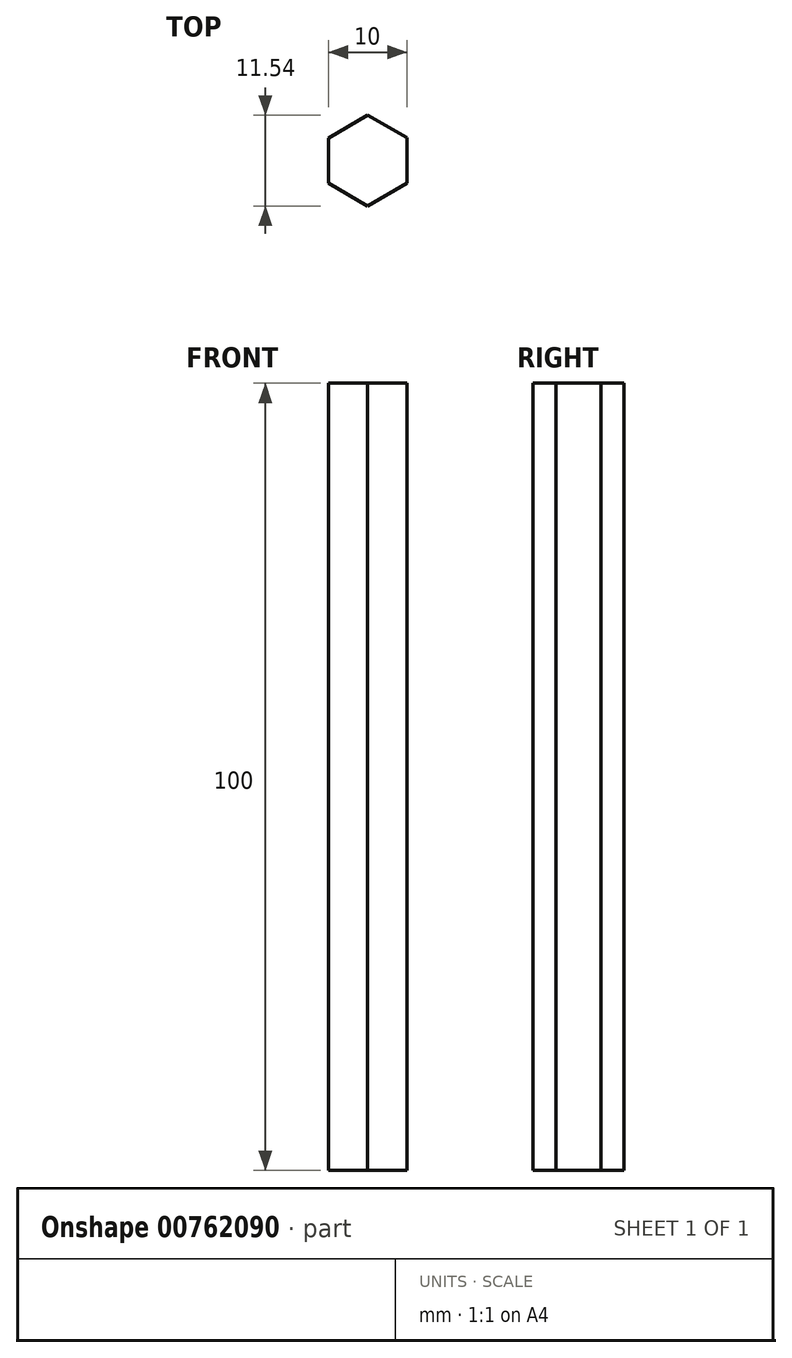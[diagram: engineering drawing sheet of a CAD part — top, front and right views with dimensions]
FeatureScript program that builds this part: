
annotation { "Feature Type Name" : "Feature", "Feature Type Description" : "" }
export const myFeature = defineFeature(function(context is Context, id is Id, definition is map)
    precondition{}
    {
        {
            var Q0;
            Q0=qCreatedBy(makeId("Top.planeOp"),FACE);
            var sketch = newSketch(context, id + "F0", { "sketchPlane" : qUnion([Q0])});
            skCircle(sketch, "E0.cCircle", {"center": v(0, 0) * mm, "radius": 5 * mm, "construction": true});
            skLineSegment(sketch, "E0.0", {"start": v(5, -2.88) * mm, "end": v(0, -5.77) * mm});
            skLineSegment(sketch, "E0.1", {"start": v(0, -5.77) * mm, "end": v(-5, -2.9) * mm});
            skLineSegment(sketch, "E0.2", {"start": v(-5, -2.9) * mm, "end": v(-5, 2.88) * mm});
            skLineSegment(sketch, "E0.3", {"start": v(-5, 2.88) * mm, "end": v(0, 5.77) * mm});
            skLineSegment(sketch, "E0.4", {"start": v(0, 5.77) * mm, "end": v(5, 2.9) * mm});
            skLineSegment(sketch, "E0.5", {"start": v(5, 2.9) * mm, "end": v(5, -2.88) * mm});
            skPoint(sketch, "E0.0.midPoint", {"position": v(2.5, -4.33) * mm});
            skSolve(sketch);
        }
        {
            var Q0;
            Q0 = qSketchRegion(id + "F0", true);
            extrude(context, id + "F1", {"entities" : qUnion([Q0]), "depth" : 100 * mm, "offsetDistance" : 25 * mm});
        }
    });
